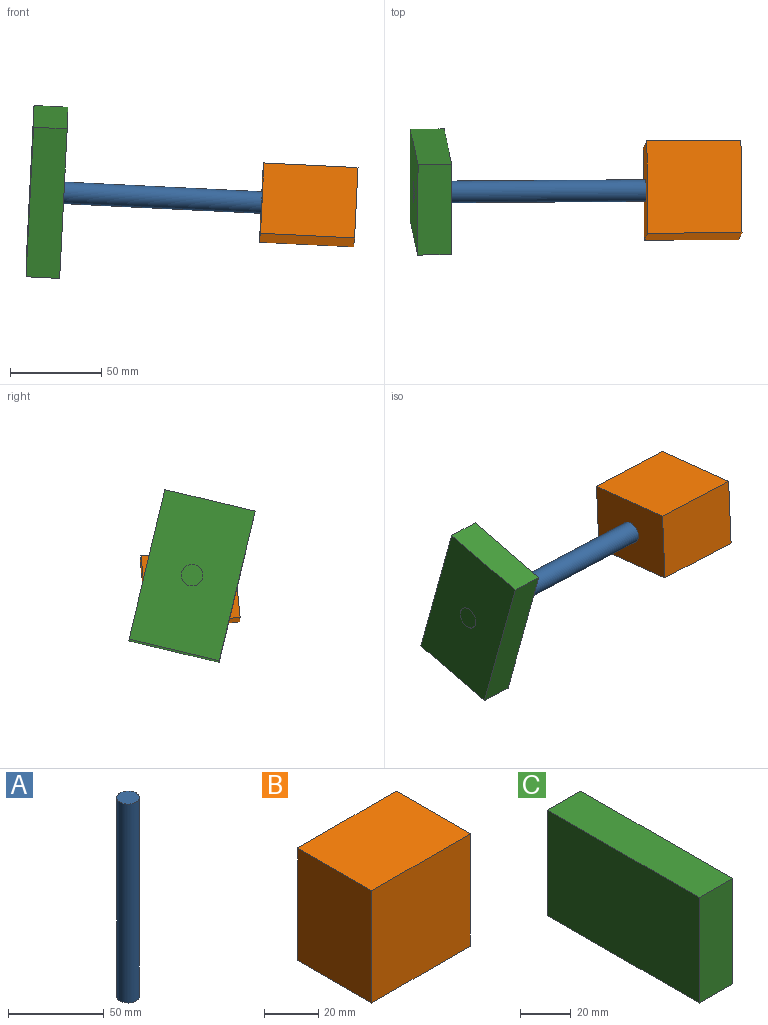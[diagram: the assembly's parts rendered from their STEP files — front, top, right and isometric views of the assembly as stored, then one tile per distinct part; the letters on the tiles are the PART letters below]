
ASSEMBLY  parts=3 mates=2
PART A: 3 faces, bbox 11.9x11.9x127 mm
  f0: cylinder r=5.93mm len=127mm, axis (0,0,-1), area 4733.4mm2, adj f1,f2
  f1: plane 11.86x11.86mm, normal (0,0,1), area 110.5mm2, adj f0
  f2: plane 11.86x11.86mm, normal (0,0,-1), area 110.5mm2, adj f0
PART B: 6 faces, bbox 51.6x38.7x50.8 mm
  f0: plane 51.58x50.8mm, normal (0,1,0), area 2620.2mm2, adj f1,f3,f4,f5
  f1: plane 50.8x38.74mm, normal (-1,0,0), area 1967.8mm2, adj f0,f2,f4,f5
  f2: plane 51.58x50.8mm, normal (0,-1,0), area 2620.2mm2, adj f1,f3,f4,f5
  f3: plane 50.8x38.74mm, normal (1,0,0), area 1967.8mm2, adj f0,f2,f4,f5
  f4: plane 51.58x38.74mm, normal (0,0,1), area 1998mm2, adj f0,f1,f2,f3
  f5: plane 51.58x38.74mm, normal (0,0,-1), area 1998mm2, adj f0,f1,f2,f3
PART C: 6 faces, bbox 18.4x84.3x50.8 mm
  f0: plane 50.8x18.44mm, normal (0,1,0), area 936.6mm2, adj f1,f3,f4,f5
  f1: plane 84.31x50.8mm, normal (-1,0,0), area 4282.9mm2, adj f0,f2,f4,f5
  f2: plane 50.8x18.44mm, normal (0,-1,0), area 936.6mm2, adj f1,f3,f4,f5
  f3: plane 84.31x50.8mm, normal (1,0,0), area 4282.9mm2, adj f0,f2,f4,f5
  f4: plane 84.31x18.44mm, normal (0,0,1), area 1554.3mm2, adj f0,f1,f2,f3
  f5: plane 84.31x18.44mm, normal (0,0,-1), area 1554.3mm2, adj f0,f1,f2,f3
PLACE A rot(axis=(-0.61,0.55,-0.57),124.4deg) t=(-159.59,31.21,43.64)mm
PLACE B rot(axis=(0.02,-0.67,0.74),178.4deg) t=(-32.1,59.23,54.22)mm
PLACE C rot(axis=(-1,0.03,0.03),76.6deg) t=(-101.85,6.25,37.61)mm
MATE revolute B.f3 <-> A.f0  axis (-1,-0.01,0.05) through (-32.74,32.08,37.41)mm
MATE revolute C.f1 <-> A.f0  axis (-1,-0.01,0.05) through (-159.59,31.21,43.64)mm
